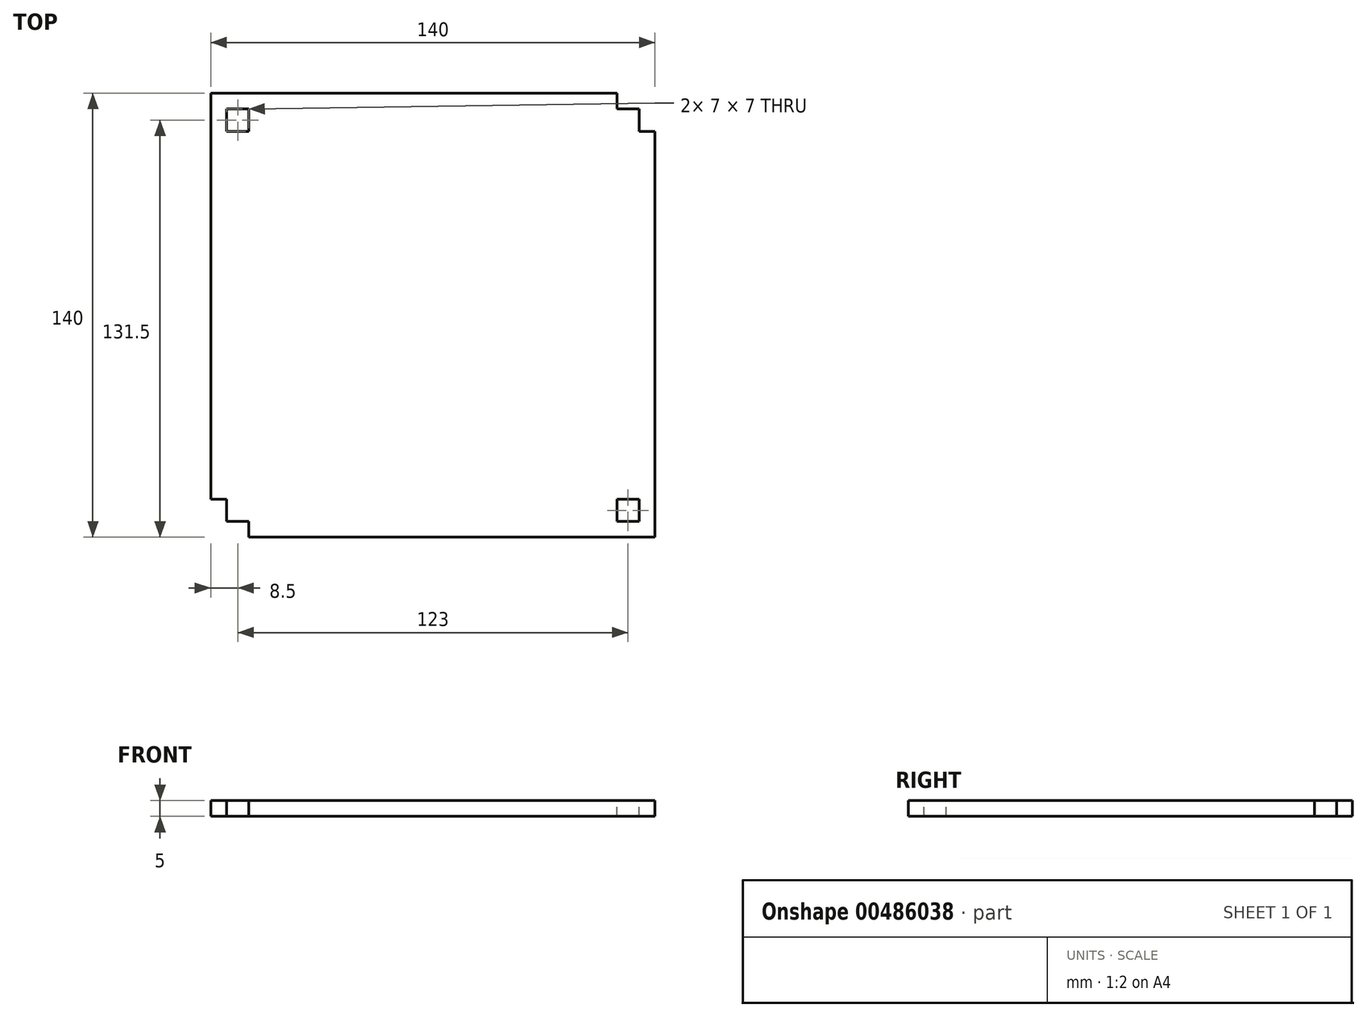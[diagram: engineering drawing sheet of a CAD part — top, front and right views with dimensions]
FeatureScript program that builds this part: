
annotation { "Feature Type Name" : "Feature", "Feature Type Description" : "" }
export const myFeature = defineFeature(function(context is Context, id is Id, definition is map)
    precondition{}
    {
        {
            var Q0;
            Q0=qCreatedBy(makeId("Top.planeOp"),FACE);
            var sketch = newSketch(context, id + "F0", { "sketchPlane" : qUnion([Q0])});
            skLineSegment(sketch, "E0.bottom", {"start": v(70, 70) * mm, "end": v(-70, 70) * mm});
            skLineSegment(sketch, "E0.top", {"start": v(70, -70) * mm, "end": v(-70, -70) * mm});
            skLineSegment(sketch, "E0.left", {"start": v(70, 70) * mm, "end": v(70, -70) * mm});
            skLineSegment(sketch, "E0.right", {"start": v(-70, 70) * mm, "end": v(-70, -70) * mm});
            skPoint(sketch, "E0.middle", {"position": v(0, 0) * mm});
            skSolve(sketch);
        }
        {
            var Q0;
            Q0=makeQuery(id+"F0.imprint","IMPRINT",FACE,{"disambiguationData":[TD([[makeQuery(id+"F0.imprint","IMPRINT",EDGE,{"derivedFrom":sQuery(id+"F0.wireOp",EDGE,"E0.bottom")}),1.0]])]});
            extrude(context, id + "F1", {"entities" : qUnion([Q0]), "depth" : 5 * mm});
        }
        {
            var Q0;
            Q0=makeQuery(id+"F1.opExtrude","CAP_FACE",FACE,{"disambiguationData":[OSD([sQuery(id+"F0.wireOp",EDGE,"E0.bottom"),sQuery(id+"F0.wireOp",EDGE,"E0.top"),sQuery(id+"F0.wireOp",EDGE,"E0.left"),sQuery(id+"F0.wireOp",EDGE,"E0.right")])],"isStart":false});
            var sketch = newSketch(context, id + "F2", { "sketchPlane" : qUnion([Q0])});
            skLineSegment(sketch, "E1.bottom", {"start": v(-70, 58) * mm, "end": v(-58, 58) * mm});
            skLineSegment(sketch, "E1.top", {"start": v(-70, 70) * mm, "end": v(-58, 70) * mm});
            skLineSegment(sketch, "E1.left", {"start": v(-70, 58) * mm, "end": v(-70, 70) * mm});
            skLineSegment(sketch, "E1.right", {"start": v(-58, 58) * mm, "end": v(-58, 70) * mm});
            skLineSegment(sketch, "E2.bottom", {"start": v(-65, 58) * mm, "end": v(-58, 58) * mm});
            skLineSegment(sketch, "E2.top", {"start": v(-65, 65) * mm, "end": v(-58, 65) * mm});
            skLineSegment(sketch, "E2.left", {"start": v(-65, 58) * mm, "end": v(-65, 65) * mm});
            skLineSegment(sketch, "E2.right", {"start": v(-58, 58) * mm, "end": v(-58, 65) * mm});
            skLineSegment(sketch, "E3.MirrorCS", {"start": v(58, 58) * mm, "end": v(58, 65) * mm});
            skLineSegment(sketch, "E4.MirrorCS", {"start": v(65, 58) * mm, "end": v(65, 65) * mm});
            skLineSegment(sketch, "E5.MirrorCS", {"start": v(65, 65) * mm, "end": v(58, 65) * mm});
            skLineSegment(sketch, "E6.MirrorCS", {"start": v(65, 58) * mm, "end": v(58, 58) * mm});
            skLineSegment(sketch, "E7.MirrorCS", {"start": v(58, 58) * mm, "end": v(58, 70) * mm});
            skLineSegment(sketch, "E8.MirrorCS", {"start": v(70, 58) * mm, "end": v(70, 70) * mm});
            skLineSegment(sketch, "E9.MirrorCS", {"start": v(70, 70) * mm, "end": v(58, 70) * mm});
            skLineSegment(sketch, "E10.MirrorCS", {"start": v(70, 58) * mm, "end": v(58, 58) * mm});
            skLineSegment(sketch, "E11.MirrorCS", {"start": v(-65, -65) * mm, "end": v(-58, -65) * mm});
            skLineSegment(sketch, "E12.MirrorCS", {"start": v(-65, -58) * mm, "end": v(-58, -58) * mm});
            skLineSegment(sketch, "E13.MirrorCS", {"start": v(-70, -58) * mm, "end": v(-58, -58) * mm});
            skLineSegment(sketch, "E14.MirrorCS", {"start": v(70, -58) * mm, "end": v(58, -58) * mm});
            skLineSegment(sketch, "E15.MirrorCS", {"start": v(65, -65) * mm, "end": v(58, -65) * mm});
            skLineSegment(sketch, "E16.MirrorCS", {"start": v(65, -58) * mm, "end": v(58, -58) * mm});
            skLineSegment(sketch, "E17.MirrorCS", {"start": v(-70, -70) * mm, "end": v(-58, -70) * mm});
            skLineSegment(sketch, "E18.MirrorCS", {"start": v(-58, -58) * mm, "end": v(-58, -65) * mm});
            skLineSegment(sketch, "E19.MirrorCS", {"start": v(58, -58) * mm, "end": v(58, -65) * mm});
            skLineSegment(sketch, "E20.MirrorCS", {"start": v(-65, -58) * mm, "end": v(-65, -65) * mm});
            skLineSegment(sketch, "E21.MirrorCS", {"start": v(-58, -58) * mm, "end": v(-58, -70) * mm});
            skLineSegment(sketch, "E22.MirrorCS", {"start": v(-70, -58) * mm, "end": v(-70, -70) * mm});
            skLineSegment(sketch, "E23.MirrorCS", {"start": v(70, -70) * mm, "end": v(58, -70) * mm});
            skLineSegment(sketch, "E24.MirrorCS", {"start": v(70, -58) * mm, "end": v(70, -70) * mm});
            skLineSegment(sketch, "E25.MirrorCS", {"start": v(65, -58) * mm, "end": v(65, -65) * mm});
            skLineSegment(sketch, "E26.MirrorCS", {"start": v(58, -58) * mm, "end": v(58, -70) * mm});
            skSolve(sketch);
        }
        {
            var Q0;
            Q0=makeQuery(id+"F2.imprint","IMPRINT",FACE,{"disambiguationData":[TD([[makeQuery(id+"F2.imprint","IMPRINT",EDGE,{"derivedFrom":sQuery(id+"F2.wireOp",EDGE,"E1.bottom")}),1.0]])]});
            var Q1;
            {var subQ4=sQuery(id+"F2.wireOp",EDGE,"E4.MirrorCS");Q1=makeQuery(id+"F2.imprint","IMPRINT",FACE,{"disambiguationData":[TD([[makeQuery(id+"F2.imprint","IMPRINT",EDGE,{"derivedFrom":subQ4}),-1.0]])]});}
            var Q2;
            Q2=makeQuery(id+"F2.imprint","IMPRINT",FACE,{"disambiguationData":[TD([[makeQuery(id+"F2.imprint","IMPRINT",EDGE,{"derivedFrom":sQuery(id+"F2.wireOp",EDGE,"E14.MirrorCS")}),1.0]])]});
            var Q3;
            {var subQ4=sQuery(id+"F2.wireOp",EDGE,"E11.MirrorCS");Q3=makeQuery(id+"F2.imprint","IMPRINT",FACE,{"disambiguationData":[TD([[makeQuery(id+"F2.imprint","IMPRINT",EDGE,{"derivedFrom":subQ4}),-1.0]])]});}
            extrude(context, id + "F3", {"entities" : qUnion([Q0, Q1, Q2, Q3]), "operationType" : NewBodyOperationType.REMOVE, "endBound" : BoundingType.THROUGH_ALL, "oppositeDirection" : true, "depth" : 25 * mm});
        }
    });
